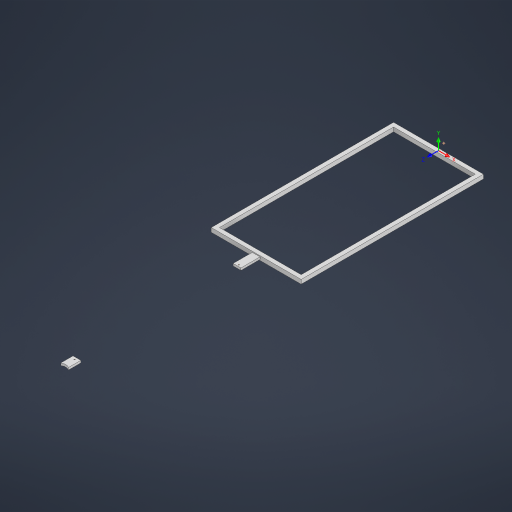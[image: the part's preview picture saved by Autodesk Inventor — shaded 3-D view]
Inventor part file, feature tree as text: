
AUTODESK INVENTOR PART (.ipt)
format: ipt  version: 2024 (Build 280153000, 153)  size: 239,616 bytes
history: native  units: mm
features: other x13, sketch x5, extrude x4, plane x1
ambient origin geometry x8: Origin, YZ Plane, XZ Plane, XY Plane, X Axis, Y Axis, Z Axis, Center Point
bodies: Body1 (feature_tree)
feature tree (23):
  other  "Sólido1"
  sketch  "Boceto2"  dims[d16=105.8mm d17=81.0mm]
  extrude  "Extrusión1"  Depth=81.0mm
  extrude  "Extrusión2"  Depth=28.4mm
  extrude  "Extrusión3"  Depth=150.0mm
  extrude  "Extrusión4"  TaperAngle=0.0deg  [1 undecoded]
  plane  "Plano de trabajo1"
  sketch  "Boceto5"  dims[d23=150.0mm d24=0.0mm]
  other  "Punto de trabajo1"
  other  "Punto de trabajo2"
  other  "Punto de trabajo3"
  other  "Punto de trabajo4"
  sketch  "Boceto6"  dims[d25=15.0mm d26=0.0mm d27=8.0mm d28=0.0mm d29=15.0mm d30=15.0mm d31=15.0mm d32=15.0mm d33=15.0mm d34=0.0mm d35=70.0mm d36=45.0mm d37=4.0mm d38=4.0mm d39=15.0mm d40=0.0mm d41=164.2mm d42=7.5mm d43=0.0mm d44=0.0mm d45=0.0mm d46=0.0mm d47=0.0mm d48=0.0mm d49=666.0mm]
  other  "SCU1"
  sketch  "Boceto3"  dims[d18=700.0mm d19=28.4mm]
  sketch  "Boceto4"  dims[d21=666.0mm d22=150.0mm]
  other  "SCU1: Plano YZ"
  other  "SCU1: Plano XZ"
  other  "SCU1: Plano XY"
  other  "SCU1: Eje X"
  other  "SCU1: Eje Y"
  other  "SCU1: Eje Z"
  other  "SCU1: Centro"
note: 1 required parameter value undecoded (feature->parameter linkage not recoverable at this tier; creation-order binding heuristic only, values carry confidence <= 0.55)
